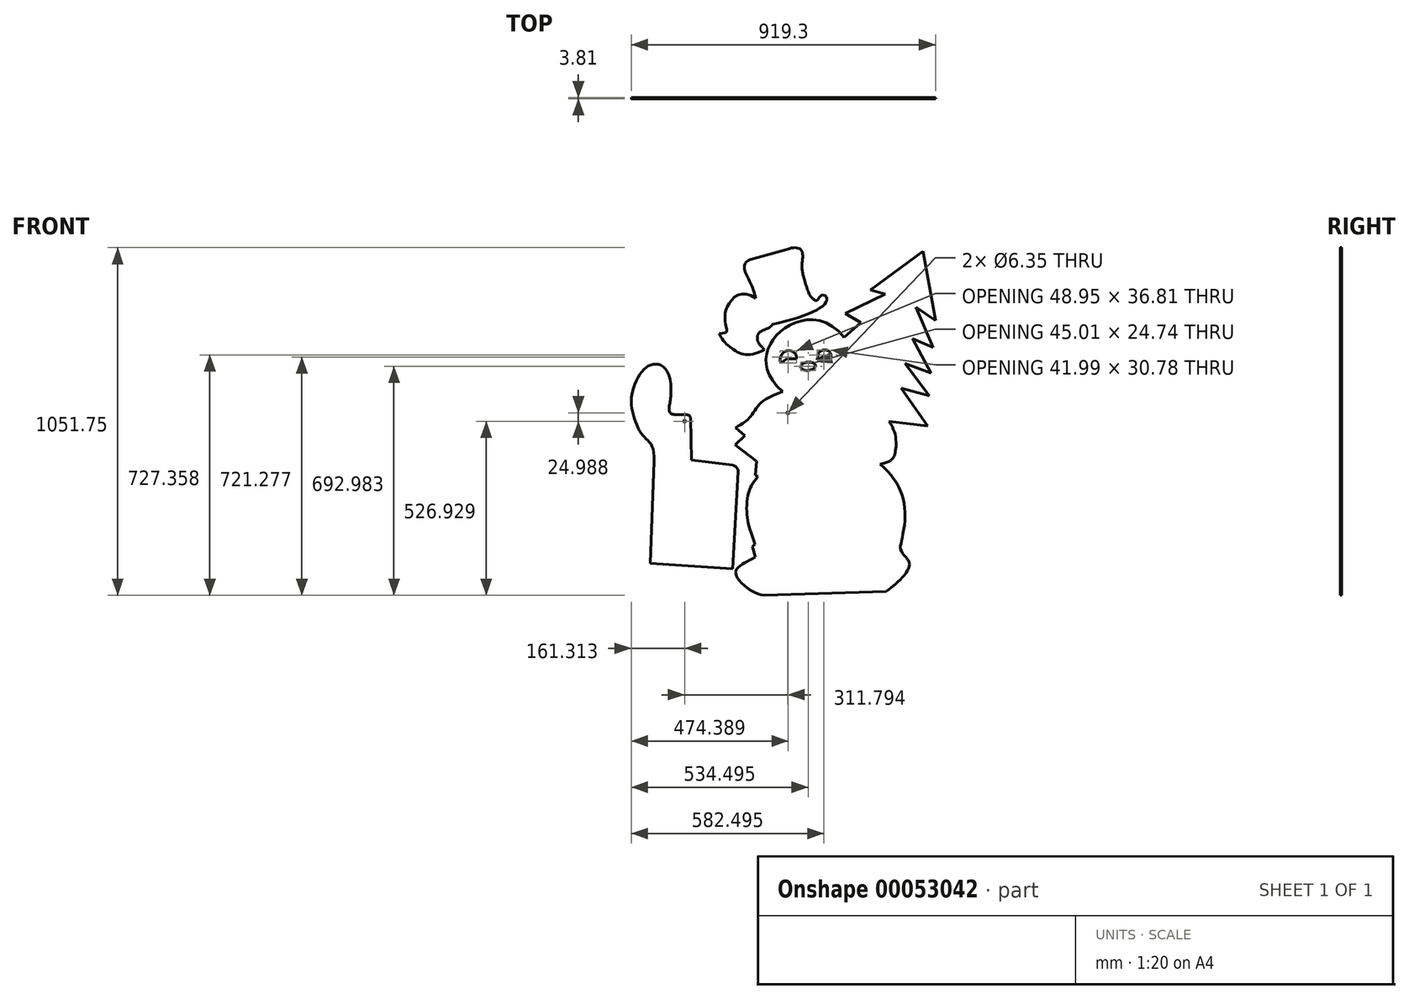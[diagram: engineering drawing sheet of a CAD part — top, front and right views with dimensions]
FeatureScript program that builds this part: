
annotation { "Feature Type Name" : "Feature", "Feature Type Description" : "" }
export const myFeature = defineFeature(function(context is Context, id is Id, definition is map)
    precondition{}
    {
        {
            var Q0;
            Q0=qCreatedBy(makeId("Front.planeOp"),FACE);
            var sketch = newSketch(context, id + "F0", { "sketchPlane" : qUnion([Q0])});
            skLineSegment(sketch, "E0", {"start": v(316.86, -336.02) * mm, "end": v(323.58, -945.59) * mm, "construction": true});
            skPoint(sketch, "E1", {"position": v(577.53, -819.37) * mm});
            skPoint(sketch, "E2", {"position": v(531.3, -696.58) * mm});
            skFitSpline(sketch, "E3", {"points": [v(577.53, -819.37) * mm, v(531.3, -696.58) * mm, v(609.32, -612.83) * mm, v(762.96, -655.17) * mm], "startDerivative": vector(-449.47, 402.2) * mm, "endDerivative": vector(385.51, -498.34) * mm});
            skLineSegment(sketch, "E4", {"start": v(316.86, -336.02) * mm, "end": v(723.24, -331.55) * mm, "construction": true});
            skPoint(sketch, "E5", {"position": v(476.24, -899.13) * mm});
            skPoint(sketch, "E6", {"position": v(508.94, -855.8) * mm});
            skPoint(sketch, "E7", {"position": v(435.18, -927.7) * mm});
            skFitSpline(sketch, "E8", {"points": [v(577.53, -819.37) * mm, v(508.94, -855.8) * mm, v(476.24, -899.13) * mm, v(435.18, -927.7) * mm], "startDerivative": vector(-230.26, -75.22) * mm, "endDerivative": vector(-190.8, -111.86) * mm});
            skPoint(sketch, "E9", {"position": v(435.43, -1367.42) * mm});
            skPoint(sketch, "E10", {"position": v(521.64, -1435.3) * mm});
            skPoint(sketch, "E11", {"position": v(889.35, -1423.14) * mm});
            skPoint(sketch, "E12", {"position": v(1000.91, -395.11) * mm});
            skLineSegment(sketch, "E13", {"start": v(889.35, -1423.14) * mm, "end": v(521.64, -1435.3) * mm});
            skLineSegment(sketch, "E14", {"start": v(435.18, -927.7) * mm, "end": v(462.66, -952.05) * mm});
            skLineSegment(sketch, "E15", {"start": v(462.66, -952.05) * mm, "end": v(433.49, -979.69) * mm});
            skLineSegment(sketch, "E16", {"start": v(433.49, -979.69) * mm, "end": v(498.3, -1030.2) * mm});
            skLineSegment(sketch, "E17", {"start": v(498.3, -1030.2) * mm, "end": v(495.26, -1071.47) * mm});
            skLineSegment(sketch, "E18", {"start": v(495.26, -1071.47) * mm, "end": v(502.65, -1075.16) * mm});
            skPoint(sketch, "E19", {"position": v(475.26, -1121.86) * mm});
            skPoint(sketch, "E20", {"position": v(469.58, -1194.68) * mm});
            skPoint(sketch, "E21", {"position": v(493.52, -1281.7) * mm});
            skFitSpline(sketch, "E22", {"points": [v(502.65, -1075.16) * mm, v(475.26, -1121.86) * mm, v(469.58, -1194.68) * mm, v(493.52, -1281.7) * mm], "startDerivative": vector(-144.57, -178.76) * mm, "endDerivative": vector(105.03, -321.04) * mm});
            skLineSegment(sketch, "E23", {"start": v(493.52, -1281.7) * mm, "end": v(485.22, -1288.04) * mm});
            skLineSegment(sketch, "E24", {"start": v(485.22, -1288.04) * mm, "end": v(494.9, -1318.72) * mm});
            skFitSpline(sketch, "E25", {"points": [v(494.9, -1318.72) * mm, v(435.43, -1367.42) * mm, v(521.64, -1435.3) * mm], "startDerivative": vector(-196.33, -117.26) * mm, "endDerivative": vector(199.23, -23.42) * mm});
            skPoint(sketch, "E26", {"position": v(933.34, -1294.87) * mm});
            skFitSpline(sketch, "E27", {"points": [v(933.34, -1294.87) * mm, v(960.25, -1345.04) * mm, v(889.35, -1423.14) * mm], "startDerivative": vector(57.7, -162.26) * mm, "endDerivative": vector(-91.37, -50.4) * mm});
            skPoint(sketch, "E28", {"position": v(871.65, -1038.35) * mm});
            skPoint(sketch, "E29", {"position": v(898.53, -908.77) * mm});
            skPoint(sketch, "E30", {"position": v(1015.83, -923.18) * mm});
            skPoint(sketch, "E31", {"position": v(917.27, -1002.94) * mm});
            skFitSpline(sketch, "E32", {"points": [v(898.53, -908.77) * mm, v(917.27, -1002.94) * mm, v(871.65, -1038.35) * mm], "startDerivative": vector(133.9, -182) * mm, "endDerivative": vector(-251.73, -48.04) * mm});
            skFitSpline(sketch, "E33", {"points": [v(871.65, -1038.35) * mm, v(947.13, -1200.06) * mm, v(933.34, -1294.87) * mm], "startDerivative": vector(289.89, -238.5) * mm, "endDerivative": vector(21.05, -59.2) * mm});
            skLineSegment(sketch, "E34", {"start": v(762.96, -655.17) * mm, "end": v(814, -610.1) * mm});
            skLineSegment(sketch, "E35", {"start": v(814, -610.1) * mm, "end": v(766.99, -582.01) * mm});
            skLineSegment(sketch, "E36", {"start": v(766.99, -582.01) * mm, "end": v(886.97, -524.07) * mm});
            skLineSegment(sketch, "E37", {"start": v(886.97, -524.07) * mm, "end": v(842.84, -511.65) * mm});
            skLineSegment(sketch, "E38", {"start": v(842.84, -511.65) * mm, "end": v(1000.91, -395.11) * mm});
            skLineSegment(sketch, "E39", {"start": v(1000.91, -395.11) * mm, "end": v(1039.02, -604.16) * mm});
            skLineSegment(sketch, "E40", {"start": v(1039.02, -604.16) * mm, "end": v(979.36, -564.08) * mm});
            skLineSegment(sketch, "E41", {"start": v(979.36, -564.08) * mm, "end": v(1032.06, -685.37) * mm});
            skLineSegment(sketch, "E42", {"start": v(1032.06, -685.37) * mm, "end": v(969.71, -659.27) * mm});
            skLineSegment(sketch, "E43", {"start": v(969.71, -659.27) * mm, "end": v(1026.26, -763.1) * mm});
            skLineSegment(sketch, "E44", {"start": v(1026.26, -763.1) * mm, "end": v(946.27, -733.76) * mm});
            skLineSegment(sketch, "E45", {"start": v(946.27, -733.76) * mm, "end": v(1020.47, -831.53) * mm});
            skLineSegment(sketch, "E46", {"start": v(1020.47, -831.53) * mm, "end": v(935.23, -808.26) * mm});
            skLineSegment(sketch, "E47", {"start": v(935.23, -808.26) * mm, "end": v(1015.83, -923.18) * mm});
            skLineSegment(sketch, "E48", {"start": v(898.53, -908.77) * mm, "end": v(1015.83, -923.18) * mm});
            skPoint(sketch, "E49", {"position": v(592.83, -883.38) * mm});
            skCircle(sketch, "E50", {"center": v(592.83, -883.38) * mm, "radius": 3.18 * mm});
            skLineSegment(sketch, "E51", {"start": v(176.67, -1338.16) * mm, "end": v(425.7, -1355.23) * mm});
            skLineSegment(sketch, "E52", {"start": v(425.7, -1355.23) * mm, "end": v(442.6, -1061.46) * mm});
            skLineSegment(sketch, "E53", {"start": v(425.92, -1041.46) * mm, "end": v(301.12, -1026.06) * mm});
            skLineSegment(sketch, "E54", {"start": v(301.12, -1026.06) * mm, "end": v(298.69, -898.83) * mm});
            skPoint(sketch, "E55.visualSharp", {"position": v(443.63, -1043.64) * mm});
            skArc(sketch, "E55.filletArc", {"start": v(442.6, -1061.46) * mm, "mid": v(438.21, -1048.16) * mm, "end": v(425.92, -1041.46) * mm});
            skLineSegment(sketch, "E56", {"start": v(188.24, -1029.5) * mm, "end": v(176.67, -1338.16) * mm});
            skPoint(sketch, "E57", {"position": v(269.82, -888.76) * mm});
            skFitSpline(sketch, "E58", {"points": [v(269.82, -888.76) * mm, v(298.69, -898.83) * mm], "startDerivative": vector(46.38, -0.67) * mm, "endDerivative": vector(3.98, -37.57) * mm});
            skPoint(sketch, "E59", {"position": v(183.61, -736.86) * mm});
            skPoint(sketch, "E60", {"position": v(239, -833.6) * mm});
            skPoint(sketch, "E61", {"position": v(120.34, -836.27) * mm});
            skFitSpline(sketch, "E62", {"points": [v(120.34, -836.27) * mm, v(183.61, -736.86) * mm, v(239, -833.6) * mm], "startDerivative": vector(57.81, 330.67) * mm, "endDerivative": vector(-40.94, -495) * mm});
            skPoint(sketch, "E63", {"position": v(149.76, -944.95) * mm});
            skFitSpline(sketch, "E64", {"points": [v(120.34, -836.27) * mm, v(149.76, -944.95) * mm, v(188.24, -1029.5) * mm], "startDerivative": vector(-21.12, -145.87) * mm, "endDerivative": vector(-23.23, -363.06) * mm});
            skFitSpline(sketch, "E65", {"points": [v(239, -833.6) * mm, v(237.8, -883.9) * mm, v(269.82, -888.76) * mm], "startDerivative": vector(-7.64, -118.45) * mm, "endDerivative": vector(55.01, -0.8) * mm});
            skPoint(sketch, "E66", {"position": v(281.03, -908.37) * mm});
            skCircle(sketch, "E67", {"center": v(281.03, -908.37) * mm, "radius": 3.18 * mm});
            skPoint(sketch, "E68", {"position": v(546.78, -615.63) * mm});
            skPoint(sketch, "E69", {"position": v(522.89, -692.32) * mm});
            skPoint(sketch, "E70", {"position": v(385.25, -642.94) * mm});
            skPoint(sketch, "E71", {"position": v(496.19, -537.1) * mm});
            skPoint(sketch, "E72", {"position": v(679.13, -544.53) * mm});
            skFitSpline(sketch, "E73", {"points": [v(679.13, -544.53) * mm, v(694.8, -528.14) * mm, v(707.8, -530.6) * mm, v(706.58, -550.78) * mm, v(546.78, -615.63) * mm], "startDerivative": vector(106.22, 93.2) * mm, "endDerivative": vector(-497.8, -111.15) * mm});
            skFitSpline(sketch, "E74", {"points": [v(546.78, -615.63) * mm, v(529.36, -629.14) * mm, v(505.97, -641.07) * mm, v(501.69, -664.77) * mm, v(522.89, -692.32) * mm], "startDerivative": vector(-98.54, -125.64) * mm, "endDerivative": vector(95.2, -81.39) * mm});
            skFitSpline(sketch, "E75", {"points": [v(385.25, -642.94) * mm, v(434.18, -695.61) * mm, v(522.89, -692.32) * mm], "startDerivative": vector(49.67, -126.76) * mm, "endDerivative": vector(236.89, 118.6) * mm});
            skFitSpline(sketch, "E76", {"points": [v(385.25, -642.94) * mm, v(408.34, -636.58) * mm, v(406.18, -620.36) * mm, v(407.26, -568.67) * mm, v(496.19, -537.1) * mm], "startDerivative": vector(275.38, 35.92) * mm, "endDerivative": vector(365.63, -275.62) * mm});
            skLineSegment(sketch, "E77", {"start": v(478.37, -419.56) * mm, "end": v(597.3, -386.4) * mm});
            skFitSpline(sketch, "E78", {"points": [v(597.3, -386.4) * mm, v(634.35, -392.3) * mm, v(635.51, -436.39) * mm, v(638.41, -464.23) * mm], "startDerivative": vector(134.91, 45.05) * mm, "endDerivative": vector(14.97, -80.38) * mm});
            skFitSpline(sketch, "E79", {"points": [v(478.37, -419.56) * mm, v(461.85, -446) * mm, v(478.37, -486.02) * mm, v(496.19, -537.1) * mm], "startDerivative": vector(-133.77, -52.25) * mm, "endDerivative": vector(42.11, -161.7) * mm});
            skFitSpline(sketch, "E80", {"points": [v(638.41, -464.23) * mm, v(661.59, -530.36) * mm, v(679.13, -544.53) * mm], "startDerivative": vector(28.96, -83.81) * mm, "endDerivative": vector(26.86, -4.57) * mm});
            skPoint(sketch, "E81", {"position": v(171.6, -762.66) * mm});
            skPoint(sketch, "E82", {"position": v(208.94, -771.37) * mm});
            skLineSegment(sketch, "E83", {"start": v(171.6, -762.66) * mm, "end": v(208.94, -771.37) * mm, "construction": true});
            skPoint(sketch, "E84", {"position": v(461.36, -691.51) * mm});
            skLineSegment(sketch, "E85", {"start": v(461.36, -691.51) * mm, "end": v(427.18, -674.12) * mm, "construction": true});
            skFitSpline(sketch, "E86", {"points": [v(571.8, -732.43) * mm, v(569.92, -716.67) * mm, v(581.92, -699.18) * mm, v(603.4, -696.1) * mm, v(617.87, -708.57) * mm, v(618.27, -719.5) * mm], "startDerivative": vector(-22.93, 80.55) * mm, "endDerivative": vector(-10.97, -67.9) * mm});
            skLineSegment(sketch, "E87", {"start": v(618.27, -719.5) * mm, "end": v(590.23, -720.2) * mm});
            skLineSegment(sketch, "E88", {"start": v(590.23, -720.2) * mm, "end": v(571.8, -732.43) * mm});
            skFitSpline(sketch, "E89", {"points": [v(681.22, -723.33) * mm, v(703.72, -714.42) * mm, v(720.31, -717.95) * mm], "startDerivative": vector(41.1, 34.43) * mm, "endDerivative": vector(39.42, -12.7) * mm});
            skFitSpline(sketch, "E90", {"points": [v(684.84, -703.12) * mm, v(715.46, -695.36) * mm, v(720.31, -717.95) * mm], "startDerivative": vector(38.8, 56.48) * mm, "endDerivative": vector(-38.48, -38.48) * mm});
            skLineSegment(sketch, "E91", {"start": v(684.84, -703.12) * mm, "end": v(681.22, -723.33) * mm});
            skFitSpline(sketch, "E92", {"points": [v(631.71, -744.97) * mm, v(653.24, -729.97) * mm, v(676.72, -740.56) * mm], "startDerivative": vector(6.75, 59.6) * mm, "endDerivative": vector(10.64, -55.33) * mm});
            skFitSpline(sketch, "E93", {"points": [v(631.71, -744.97) * mm, v(655.54, -754.68) * mm, v(676.72, -740.56) * mm], "startDerivative": vector(0, -38.02) * mm, "endDerivative": vector(-4.33, 34.62) * mm});
            skSolve(sketch);
        }
        {
            var Q0;
            Q0=makeQuery(id+"F0.imprint","IMPRINT",FACE,{"disambiguationData":[TD([[makeQuery(id+"F0.imprint","IMPRINT",EDGE,{"derivedFrom":sQuery(id+"F0.wireOp",EDGE,"E3")}),-1.0]])]});
            extrude(context, id + "F1", {"entities" : qUnion([Q0]), "depth" : 3.8 * mm});
        }
        {
            var Q0;
            Q0=makeQuery(id+"F0.imprint","IMPRINT",FACE,{"disambiguationData":[TD([[makeQuery(id+"F0.imprint","IMPRINT",EDGE,{"derivedFrom":sQuery(id+"F0.wireOp",EDGE,"E51")}),1.0]])]});
            var Q1;
            Q1=makeQuery(id+"F1.opExtrude","CAP_FACE",FACE,{"disambiguationData":[OSD([sQuery(id+"F0.wireOp",EDGE,"E3"),sQuery(id+"F0.wireOp",EDGE,"E8"),sQuery(id+"F0.wireOp",EDGE,"E13"),sQuery(id+"F0.wireOp",EDGE,"E14"),sQuery(id+"F0.wireOp",EDGE,"E15"),sQuery(id+"F0.wireOp",EDGE,"E16"),sQuery(id+"F0.wireOp",EDGE,"E17"),sQuery(id+"F0.wireOp",EDGE,"E18"),sQuery(id+"F0.wireOp",EDGE,"E22"),sQuery(id+"F0.wireOp",EDGE,"E23"),sQuery(id+"F0.wireOp",EDGE,"E24"),sQuery(id+"F0.wireOp",EDGE,"E25"),sQuery(id+"F0.wireOp",EDGE,"E27"),sQuery(id+"F0.wireOp",EDGE,"E32"),sQuery(id+"F0.wireOp",EDGE,"E33"),sQuery(id+"F0.wireOp",EDGE,"E34"),sQuery(id+"F0.wireOp",EDGE,"E35"),sQuery(id+"F0.wireOp",EDGE,"E36"),sQuery(id+"F0.wireOp",EDGE,"E37"),sQuery(id+"F0.wireOp",EDGE,"E38"),sQuery(id+"F0.wireOp",EDGE,"E39"),sQuery(id+"F0.wireOp",EDGE,"E40"),sQuery(id+"F0.wireOp",EDGE,"E41"),sQuery(id+"F0.wireOp",EDGE,"E42"),sQuery(id+"F0.wireOp",EDGE,"E43"),sQuery(id+"F0.wireOp",EDGE,"E44"),sQuery(id+"F0.wireOp",EDGE,"E45"),sQuery(id+"F0.wireOp",EDGE,"E46"),sQuery(id+"F0.wireOp",EDGE,"E47"),sQuery(id+"F0.wireOp",EDGE,"E48"),sQuery(id+"F0.wireOp",EDGE,"E50")])],"isStart":false});
            extrude(context, id + "F2", {"entities" : qUnion([Q0]), "endBound" : BoundingType.UP_TO_SURFACE, "endBoundEntityFace" : qUnion([Q1]), "depth" : 6.35 * mm});
        }
        {
            var Q0;
            Q0=makeQuery(id+"F0.imprint","IMPRINT",FACE,{"disambiguationData":[TD([[makeQuery(id+"F0.imprint","IMPRINT",EDGE,{"derivedFrom":sQuery(id+"F0.wireOp",EDGE,"E73")}),-1.0]])]});
            var Q1;
            Q1=makeQuery(id+"F1.opExtrude","CAP_FACE",FACE,{"disambiguationData":[OSD([sQuery(id+"F0.wireOp",EDGE,"E3"),sQuery(id+"F0.wireOp",EDGE,"E8"),sQuery(id+"F0.wireOp",EDGE,"E13"),sQuery(id+"F0.wireOp",EDGE,"E14"),sQuery(id+"F0.wireOp",EDGE,"E15"),sQuery(id+"F0.wireOp",EDGE,"E16"),sQuery(id+"F0.wireOp",EDGE,"E17"),sQuery(id+"F0.wireOp",EDGE,"E18"),sQuery(id+"F0.wireOp",EDGE,"E22"),sQuery(id+"F0.wireOp",EDGE,"E23"),sQuery(id+"F0.wireOp",EDGE,"E24"),sQuery(id+"F0.wireOp",EDGE,"E25"),sQuery(id+"F0.wireOp",EDGE,"E27"),sQuery(id+"F0.wireOp",EDGE,"E32"),sQuery(id+"F0.wireOp",EDGE,"E33"),sQuery(id+"F0.wireOp",EDGE,"E34"),sQuery(id+"F0.wireOp",EDGE,"E35"),sQuery(id+"F0.wireOp",EDGE,"E36"),sQuery(id+"F0.wireOp",EDGE,"E37"),sQuery(id+"F0.wireOp",EDGE,"E38"),sQuery(id+"F0.wireOp",EDGE,"E39"),sQuery(id+"F0.wireOp",EDGE,"E40"),sQuery(id+"F0.wireOp",EDGE,"E41"),sQuery(id+"F0.wireOp",EDGE,"E42"),sQuery(id+"F0.wireOp",EDGE,"E43"),sQuery(id+"F0.wireOp",EDGE,"E44"),sQuery(id+"F0.wireOp",EDGE,"E45"),sQuery(id+"F0.wireOp",EDGE,"E46"),sQuery(id+"F0.wireOp",EDGE,"E47"),sQuery(id+"F0.wireOp",EDGE,"E48"),sQuery(id+"F0.wireOp",EDGE,"E50")])],"isStart":false});
            extrude(context, id + "F3", {"entities" : qUnion([Q0]), "endBound" : BoundingType.UP_TO_SURFACE, "endBoundEntityFace" : qUnion([Q1]), "depth" : 6.35 * mm});
        }
        {
            var Q0;
            Q0=makeQuery(id+"F2.opExtrude","CAP_FACE",FACE,{"disambiguationData":[OSD([sQuery(id+"F0.wireOp",EDGE,"E51"),sQuery(id+"F0.wireOp",EDGE,"E52"),sQuery(id+"F0.wireOp",EDGE,"E53"),sQuery(id+"F0.wireOp",EDGE,"E54"),sQuery(id+"F0.wireOp",EDGE,"E55.filletArc"),sQuery(id+"F0.wireOp",EDGE,"E56"),sQuery(id+"F0.wireOp",EDGE,"E58"),sQuery(id+"F0.wireOp",EDGE,"E62"),sQuery(id+"F0.wireOp",EDGE,"E64"),sQuery(id+"F0.wireOp",EDGE,"E65"),sQuery(id+"F0.wireOp",EDGE,"E67")])],"isStart":true});
            var sketch = newSketch(context, id + "F4", { "sketchPlane" : qUnion([Q0])});
            skPoint(sketch, "E94.0", {"position": v(-281.03, -908.37) * mm});
            skArc(sketch, "E95", {"start": v(-176.9, -1331.67) * mm, "mid": v(-303.3, -1343.72) * mm, "end": v(-427.79, -1318.84) * mm, "construction": true});
            skLineSegment(sketch, "E96", {"start": v(-281.03, -908.37) * mm, "end": v(-427.79, -1318.84) * mm, "construction": true});
            skLineSegment(sketch, "E97", {"start": v(-281.03, -908.37) * mm, "end": v(-176.9, -1331.67) * mm, "construction": true});
            skLineSegment(sketch, "E98.0", {"start": v(-425.7, -1355.23) * mm, "end": v(-442.6, -1061.46) * mm, "construction": true});
            skLineSegment(sketch, "E99.0", {"start": v(-188.24, -1029.5) * mm, "end": v(-176.67, -1338.16) * mm, "construction": true});
            skLineSegment(sketch, "E100.0", {"start": v(-176.67, -1338.16) * mm, "end": v(-425.7, -1355.23) * mm, "construction": true});
            skSolve(sketch);
        }
    });
